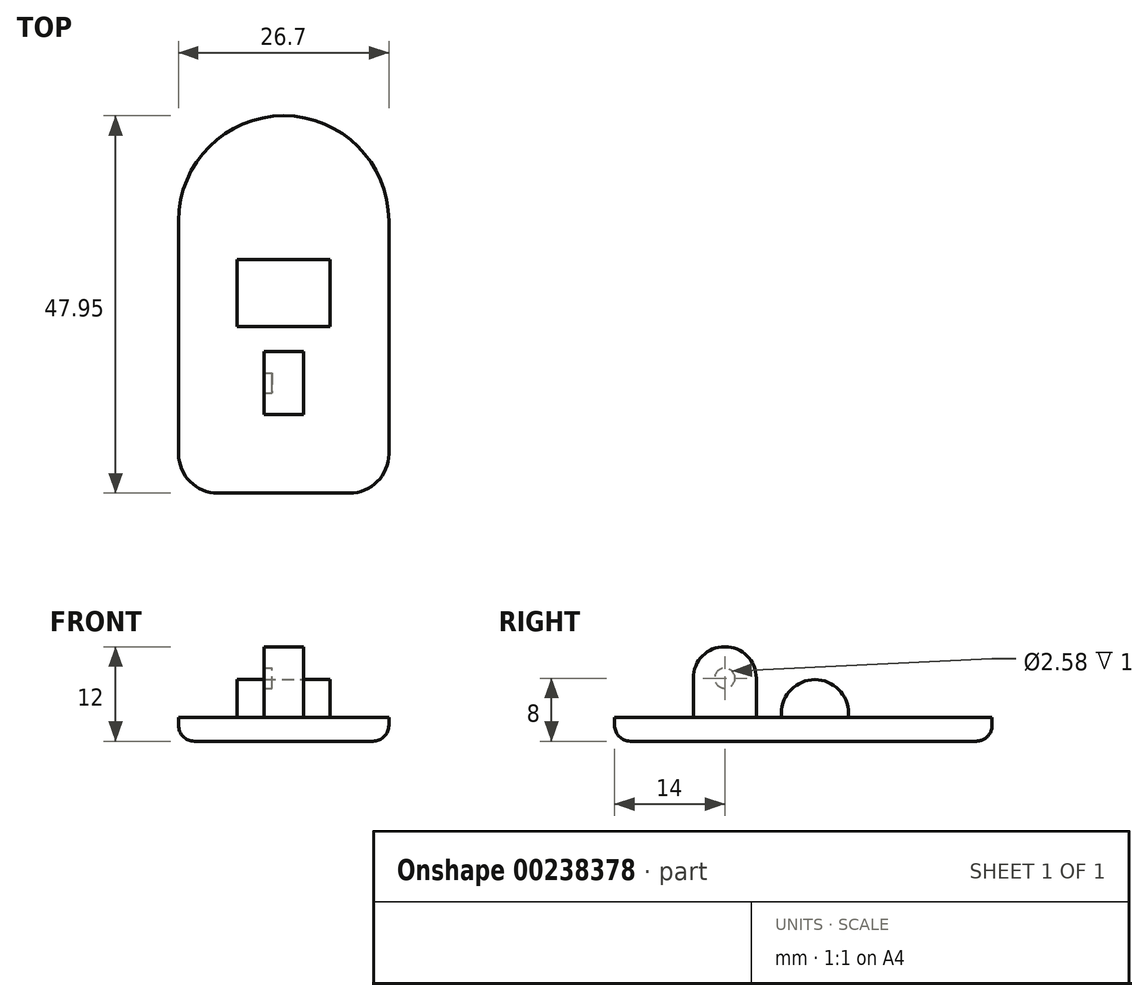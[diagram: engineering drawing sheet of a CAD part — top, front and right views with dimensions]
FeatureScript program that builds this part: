
annotation { "Feature Type Name" : "Feature", "Feature Type Description" : "" }
export const myFeature = defineFeature(function(context is Context, id is Id, definition is map)
    precondition{}
    {
        {
            var Q0;
            Q0=qCreatedBy(makeId("Top.planeOp"),FACE);
            var sketch = newSketch(context, id + "F0", { "sketchPlane" : qUnion([Q0])});
            skArc(sketch, "E0", {"start": v(13.35, 0) * mm, "mid": v(0, 13.35) * mm, "end": v(-13.35, 0) * mm});
            skLineSegment(sketch, "E1", {"start": v(-13.35, 0) * mm, "end": v(-13.35, -34.6) * mm});
            skLineSegment(sketch, "E2", {"start": v(13.35, 0) * mm, "end": v(13.35, -34.6) * mm});
            skLineSegment(sketch, "E3", {"start": v(13.35, -34.6) * mm, "end": v(-13.35, -34.6) * mm});
            skLineSegment(sketch, "E4", {"start": v(0, -34.6) * mm, "end": v(0, 13.35) * mm});
            skLineSegment(sketch, "E5", {"start": v(-13.35, -24.6) * mm, "end": v(13.35, -24.6) * mm});
            skLineSegment(sketch, "E6", {"start": v(-13.35, -16.6) * mm, "end": v(13.35, -16.6) * mm});
            skLineSegment(sketch, "E7", {"start": v(-2.5, -16.6) * mm, "end": v(-2.5, -34.6) * mm});
            skLineSegment(sketch, "E8", {"start": v(2.5, -16.6) * mm, "end": v(2.5, -34.6) * mm});
            skPoint(sketch, "E9.orphan", {"position": v(-2.5, 0) * mm});
            skPoint(sketch, "E10.orphan", {"position": v(2.5, 0) * mm});
            skLineSegment(sketch, "E11", {"start": v(-5.9, 0) * mm, "end": v(-5.9, -16.6) * mm});
            skLineSegment(sketch, "E12", {"start": v(5.9, 0) * mm, "end": v(5.9, -16.6) * mm});
            skLineSegment(sketch, "E13", {"start": v(-13.35, -4.9) * mm, "end": v(13.35, -4.9) * mm});
            skLineSegment(sketch, "E14", {"start": v(-13.35, -13.4) * mm, "end": v(13.35, -13.4) * mm});
            skSolve(sketch);
        }
        {
            var Q0;
            {var subQ4=sQuery(id+"F0.wireOp",EDGE,"E1");var subQ6=sQuery(id+"F0.wireOp",EDGE,"E5");var subQ7=makeQuery(id+"F0.imprint","INTERSECT",VERTEX,{"derivedFrom":[subQ4,subQ6]});Q0=makeQuery(id+"F0.imprint","IMPRINT",FACE,{"disambiguationData":[TD([[makeQuery(id+"F0.imprint","IMPRINT",EDGE,{"disambiguationData":[TD([[subQ7,1.0]])],"derivedFrom":subQ4}),1.0]])]});}
            var Q1;
            {var subQ0=sQuery(id+"F0.wireOp",EDGE,"E3");var subQ1=sQuery(id+"F0.wireOp",EDGE,"E1");var subQ2=makeQuery(id+"F0.imprint","INTERSECT",VERTEX,{"derivedFrom":[subQ1,subQ0]});Q1=makeQuery(id+"F0.imprint","IMPRINT",FACE,{"disambiguationData":[TD([[makeQuery(id+"F0.imprint","IMPRINT",EDGE,{"disambiguationData":[TD([[subQ2,1.0]])],"derivedFrom":subQ1}),1.0]])]});}
            var Q2;
            {var subQ0=sQuery(id+"F0.wireOp",EDGE,"E4");var subQ1=sQuery(id+"F0.wireOp",EDGE,"E3");var subQ2=makeQuery(id+"F0.imprint","INTERSECT",VERTEX,{"derivedFrom":[subQ1,subQ0]});Q2=makeQuery(id+"F0.imprint","IMPRINT",FACE,{"disambiguationData":[TD([[makeQuery(id+"F0.imprint","IMPRINT",EDGE,{"disambiguationData":[TD([[subQ2,1.0]])],"derivedFrom":subQ1}),-1.0]])]});}
            var Q3;
            {var subQ0=sQuery(id+"F0.wireOp",EDGE,"E4");var subQ1=sQuery(id+"F0.wireOp",EDGE,"E3");var subQ2=makeQuery(id+"F0.imprint","INTERSECT",VERTEX,{"derivedFrom":[subQ1,subQ0]});Q3=makeQuery(id+"F0.imprint","IMPRINT",FACE,{"disambiguationData":[TD([[makeQuery(id+"F0.imprint","IMPRINT",EDGE,{"disambiguationData":[TD([[subQ2,-1.0]])],"derivedFrom":subQ1}),-1.0]])]});}
            var Q4;
            {var subQ0=sQuery(id+"F0.wireOp",EDGE,"E5");var subQ1=sQuery(id+"F0.wireOp",EDGE,"E4");var subQ2=makeQuery(id+"F0.imprint","INTERSECT",VERTEX,{"derivedFrom":[subQ1,subQ0]});Q4=makeQuery(id+"F0.imprint","IMPRINT",FACE,{"disambiguationData":[TD([[makeQuery(id+"F0.imprint","IMPRINT",EDGE,{"disambiguationData":[TD([[subQ2,-1.0]])],"derivedFrom":subQ1}),1.0]])]});}
            var Q5;
            {var subQ0=sQuery(id+"F0.wireOp",EDGE,"E5");var subQ1=sQuery(id+"F0.wireOp",EDGE,"E4");var subQ2=makeQuery(id+"F0.imprint","INTERSECT",VERTEX,{"derivedFrom":[subQ1,subQ0]});Q5=makeQuery(id+"F0.imprint","IMPRINT",FACE,{"disambiguationData":[TD([[makeQuery(id+"F0.imprint","IMPRINT",EDGE,{"disambiguationData":[TD([[subQ2,-1.0]])],"derivedFrom":subQ1}),-1.0]])]});}
            var Q6;
            {var subQ1=sQuery(id+"F0.wireOp",EDGE,"E2");var subQ4=sQuery(id+"F0.wireOp",EDGE,"E5");var subQ5=makeQuery(id+"F0.imprint","INTERSECT",VERTEX,{"derivedFrom":[subQ1,subQ4]});Q6=makeQuery(id+"F0.imprint","IMPRINT",FACE,{"disambiguationData":[TD([[makeQuery(id+"F0.imprint","IMPRINT",EDGE,{"disambiguationData":[TD([[subQ5,1.0]])],"derivedFrom":subQ1}),-1.0]])]});}
            var Q7;
            {var subQ0=sQuery(id+"F0.wireOp",EDGE,"E3");var subQ1=sQuery(id+"F0.wireOp",EDGE,"E2");var subQ2=makeQuery(id+"F0.imprint","INTERSECT",VERTEX,{"derivedFrom":[subQ1,subQ0]});Q7=makeQuery(id+"F0.imprint","IMPRINT",FACE,{"disambiguationData":[TD([[makeQuery(id+"F0.imprint","IMPRINT",EDGE,{"disambiguationData":[TD([[subQ2,1.0]])],"derivedFrom":subQ1}),-1.0]])]});}
            var Q8;
            {var subQ0=sQuery(id+"F0.wireOp",EDGE,"E6");var subQ4=sQuery(id+"F0.wireOp",EDGE,"E4");var subQ5=makeQuery(id+"F0.imprint","INTERSECT",VERTEX,{"derivedFrom":[subQ4,subQ0]});Q8=makeQuery(id+"F0.imprint","IMPRINT",FACE,{"disambiguationData":[TD([[makeQuery(id+"F0.imprint","IMPRINT",EDGE,{"disambiguationData":[TD([[subQ5,-1.0]])],"derivedFrom":subQ4}),-1.0]])]});}
            var Q9;
            {var subQ0=sQuery(id+"F0.wireOp",EDGE,"E6");var subQ1=sQuery(id+"F0.wireOp",EDGE,"E2");var subQ2=makeQuery(id+"F0.imprint","INTERSECT",VERTEX,{"derivedFrom":[subQ1,subQ0]});Q9=makeQuery(id+"F0.imprint","IMPRINT",FACE,{"disambiguationData":[TD([[makeQuery(id+"F0.imprint","IMPRINT",EDGE,{"disambiguationData":[TD([[subQ2,1.0]])],"derivedFrom":subQ1}),-1.0]])]});}
            var Q10;
            {var subQ1=sQuery(id+"F0.wireOp",EDGE,"E6");var subQ6=sQuery(id+"F0.wireOp",EDGE,"E4");var subQ7=makeQuery(id+"F0.imprint","INTERSECT",VERTEX,{"derivedFrom":[subQ6,subQ1]});Q10=makeQuery(id+"F0.imprint","IMPRINT",FACE,{"disambiguationData":[TD([[makeQuery(id+"F0.imprint","IMPRINT",EDGE,{"disambiguationData":[TD([[subQ7,-1.0]])],"derivedFrom":subQ6}),1.0]])]});}
            var Q11;
            {var subQ0=sQuery(id+"F0.wireOp",EDGE,"E6");var subQ1=sQuery(id+"F0.wireOp",EDGE,"E1");var subQ2=makeQuery(id+"F0.imprint","INTERSECT",VERTEX,{"derivedFrom":[subQ1,subQ0]});Q11=makeQuery(id+"F0.imprint","IMPRINT",FACE,{"disambiguationData":[TD([[makeQuery(id+"F0.imprint","IMPRINT",EDGE,{"disambiguationData":[TD([[subQ2,1.0]])],"derivedFrom":subQ1}),1.0]])]});}
            var Q12;
            {var subQ0=sQuery(id+"F0.wireOp",EDGE,"E13");var subQ1=sQuery(id+"F0.wireOp",EDGE,"E1");var subQ2=makeQuery(id+"F0.imprint","INTERSECT",VERTEX,{"derivedFrom":[subQ1,subQ0]});Q12=makeQuery(id+"F0.imprint","IMPRINT",FACE,{"disambiguationData":[TD([[makeQuery(id+"F0.imprint","IMPRINT",EDGE,{"disambiguationData":[TD([[subQ2,-1.0]])],"derivedFrom":subQ1}),1.0]])]});}
            var Q13;
            {var subQ0=sQuery(id+"F0.wireOp",EDGE,"E14");var subQ1=sQuery(id+"F0.wireOp",EDGE,"E4");var subQ2=makeQuery(id+"F0.imprint","INTERSECT",VERTEX,{"derivedFrom":[subQ1,subQ0]});Q13=makeQuery(id+"F0.imprint","IMPRINT",FACE,{"disambiguationData":[TD([[makeQuery(id+"F0.imprint","IMPRINT",EDGE,{"disambiguationData":[TD([[subQ2,-1.0]])],"derivedFrom":subQ1}),1.0]])]});}
            var Q14;
            {var subQ0=sQuery(id+"F0.wireOp",EDGE,"E14");var subQ1=sQuery(id+"F0.wireOp",EDGE,"E4");var subQ2=makeQuery(id+"F0.imprint","INTERSECT",VERTEX,{"derivedFrom":[subQ1,subQ0]});Q14=makeQuery(id+"F0.imprint","IMPRINT",FACE,{"disambiguationData":[TD([[makeQuery(id+"F0.imprint","IMPRINT",EDGE,{"disambiguationData":[TD([[subQ2,-1.0]])],"derivedFrom":subQ1}),-1.0]])]});}
            var Q15;
            {var subQ0=sQuery(id+"F0.wireOp",EDGE,"E13");var subQ1=sQuery(id+"F0.wireOp",EDGE,"E2");var subQ2=makeQuery(id+"F0.imprint","INTERSECT",VERTEX,{"derivedFrom":[subQ1,subQ0]});Q15=makeQuery(id+"F0.imprint","IMPRINT",FACE,{"disambiguationData":[TD([[makeQuery(id+"F0.imprint","IMPRINT",EDGE,{"disambiguationData":[TD([[subQ2,-1.0]])],"derivedFrom":subQ1}),-1.0]])]});}
            var Q16;
            {var subQ4=sQuery(id+"F0.wireOp",EDGE,"E0");var subQ6=sQuery(id+"F0.wireOp",EDGE,"E2");var subQ7=makeQuery(id+"F0.imprint","INTERSECT",VERTEX,{"derivedFrom":[subQ4,subQ6]});Q16=makeQuery(id+"F0.imprint","IMPRINT",FACE,{"disambiguationData":[TD([[makeQuery(id+"F0.imprint","IMPRINT",EDGE,{"disambiguationData":[TD([[subQ7,-1.0]])],"derivedFrom":subQ4}),1.0]])]});}
            var Q17;
            {var subQ1=sQuery(id+"F0.wireOp",EDGE,"E0");var subQ5=sQuery(id+"F0.wireOp",EDGE,"E1");var subQ8=makeQuery(id+"F0.imprint","INTERSECT",VERTEX,{"derivedFrom":[subQ1,subQ5]});Q17=makeQuery(id+"F0.imprint","IMPRINT",FACE,{"disambiguationData":[TD([[makeQuery(id+"F0.imprint","IMPRINT",EDGE,{"disambiguationData":[TD([[subQ8,1.0]])],"derivedFrom":subQ1}),1.0]])]});}
            extrude(context, id + "F1", {"entities" : qUnion([Q0, Q1, Q2, Q3, Q4, Q5, Q6, Q7, Q8, Q9, Q10, Q11, Q12, Q13, Q14, Q15, Q16, Q17]), "oppositeDirection" : true, "depth" : 3 * mm});
        }
        {
            var Q0;
            {var subQ0=sQuery(id+"F0.wireOp",EDGE,"E14");var subQ1=sQuery(id+"F0.wireOp",EDGE,"E4");var subQ2=makeQuery(id+"F0.imprint","INTERSECT",VERTEX,{"derivedFrom":[subQ1,subQ0]});Q0=makeQuery(id+"F0.imprint","IMPRINT",FACE,{"disambiguationData":[TD([[makeQuery(id+"F0.imprint","IMPRINT",EDGE,{"disambiguationData":[TD([[subQ2,-1.0]])],"derivedFrom":subQ1}),1.0]])]});}
            var Q1;
            {var subQ0=sQuery(id+"F0.wireOp",EDGE,"E14");var subQ1=sQuery(id+"F0.wireOp",EDGE,"E4");var subQ2=makeQuery(id+"F0.imprint","INTERSECT",VERTEX,{"derivedFrom":[subQ1,subQ0]});Q1=makeQuery(id+"F0.imprint","IMPRINT",FACE,{"disambiguationData":[TD([[makeQuery(id+"F0.imprint","IMPRINT",EDGE,{"disambiguationData":[TD([[subQ2,-1.0]])],"derivedFrom":subQ1}),-1.0]])]});}
            extrude(context, id + "F2", {"entities" : qUnion([Q0, Q1]), "operationType" : NewBodyOperationType.ADD, "depth" : .563 * mm});
        }
        {
            var Q0;
            {var subQ0=sQuery(id+"F0.wireOp",EDGE,"E5");var subQ1=sQuery(id+"F0.wireOp",EDGE,"E4");var subQ2=makeQuery(id+"F0.imprint","INTERSECT",VERTEX,{"derivedFrom":[subQ1,subQ0]});Q0=makeQuery(id+"F0.imprint","IMPRINT",FACE,{"disambiguationData":[TD([[makeQuery(id+"F0.imprint","IMPRINT",EDGE,{"disambiguationData":[TD([[subQ2,-1.0]])],"derivedFrom":subQ1}),-1.0]])]});}
            var Q1;
            {var subQ0=sQuery(id+"F0.wireOp",EDGE,"E5");var subQ1=sQuery(id+"F0.wireOp",EDGE,"E4");var subQ2=makeQuery(id+"F0.imprint","INTERSECT",VERTEX,{"derivedFrom":[subQ1,subQ0]});Q1=makeQuery(id+"F0.imprint","IMPRINT",FACE,{"disambiguationData":[TD([[makeQuery(id+"F0.imprint","IMPRINT",EDGE,{"disambiguationData":[TD([[subQ2,-1.0]])],"derivedFrom":subQ1}),1.0]])]});}
            extrude(context, id + "F3", {"entities" : qUnion([Q0, Q1]), "operationType" : NewBodyOperationType.ADD, "depth" : 5 * mm});
        }
        {
            var Q0;
            Q0=makeQuery(id+"F3.opExtrude","SWEPT_FACE",FACE,{"disambiguationData":[OSD([sQuery(id+"F0.wireOp",EDGE,"E8")])]});
            var sketch = newSketch(context, id + "F4", { "sketchPlane" : qUnion([Q0])});
            skCircle(sketch, "E15", {"center": v(-20.6, 5) * mm, "radius": 4 * mm});
            skCircle(sketch, "E16", {"center": v(-20.6, 5) * mm, "radius": 1.29 * mm});
            skSolve(sketch);
        }
        {
            var Q0;
            Q0=makeQuery(id+"F2.opExtrude","SWEPT_FACE",FACE,{"disambiguationData":[OSD([sQuery(id+"F0.wireOp",EDGE,"E12")])]});
            var sketch = newSketch(context, id + "F5", { "sketchPlane" : qUnion([Q0])});
            skCircle(sketch, "E17", {"center": v(-9.15, 0.56) * mm, "radius": 4.25 * mm});
            skSolve(sketch);
        }
        {
            var Q0;
            {var subQ1=sQuery(id+"F0.wireOp",EDGE,"E12");var subQ2=makeQuery(id+"F2.opExtrude","CAP_EDGE",EDGE,{"disambiguationData":[OSD([subQ1])],"isStart":false});Q0=makeQuery(id+"F5.imprint","IMPRINT",FACE,{"disambiguationData":[TD([[makeQuery(id+"F5.imprint","IMPRINT",EDGE,{"derivedFrom":subQ2}),-1.0]])]});}
            extrude(context, id + "F6", {"entities" : qUnion([Q0]), "operationType" : NewBodyOperationType.ADD, "oppositeDirection" : true, "depth" : 11.8 * mm});
        }
        {
            var Q0;
            {var subQ1=sQuery(id+"F0.wireOp",EDGE,"E8");var subQ2=makeQuery(id+"F3.opExtrude","CAP_EDGE",EDGE,{"disambiguationData":[OSD([subQ1])],"isStart":false});Q0=makeQuery(id+"F4.imprint","IMPRINT",FACE,{"disambiguationData":[TD([[makeQuery(id+"F4.imprint","IMPRINT",EDGE,{"derivedFrom":subQ2}),-1.0]])]});}
            extrude(context, id + "F7", {"entities" : qUnion([Q0]), "operationType" : NewBodyOperationType.ADD, "oppositeDirection" : true, "depth" : 5 * mm});
        }
        {
            var Q0;
            {var subQ0=sQuery(id+"F4.wireOp",EDGE,"E16");var subQ1=makeQuery(id+"F3.opExtrude","CAP_EDGE",EDGE,{"disambiguationData":[OSD([sQuery(id+"F0.wireOp",EDGE,"E8")])],"isStart":false});var subQ2=makeQuery(id+"F4.imprint","INTERSECT",VERTEX,{"disambiguationData":[OD(0.0)],"derivedFrom":[subQ1,subQ0]});Q0=makeQuery(id+"F4.imprint","IMPRINT",FACE,{"disambiguationData":[TD([[makeQuery(id+"F4.imprint","IMPRINT",EDGE,{"disambiguationData":[TD([[subQ2,1.0]])],"derivedFrom":subQ0}),1.0]])]});}
            var Q1;
            {var subQ0=sQuery(id+"F4.wireOp",EDGE,"E16");var subQ1=makeQuery(id+"F3.opExtrude","CAP_EDGE",EDGE,{"disambiguationData":[OSD([sQuery(id+"F0.wireOp",EDGE,"E8")])],"isStart":false});var subQ2=makeQuery(id+"F4.imprint","INTERSECT",VERTEX,{"disambiguationData":[OD(0.0)],"derivedFrom":[subQ1,subQ0]});Q1=makeQuery(id+"F4.imprint","IMPRINT",FACE,{"disambiguationData":[TD([[makeQuery(id+"F4.imprint","IMPRINT",EDGE,{"disambiguationData":[TD([[subQ2,-1.0]])],"derivedFrom":subQ0}),1.0]])]});}
            extrude(context, id + "F8", {"entities" : qUnion([Q0, Q1]), "operationType" : NewBodyOperationType.REMOVE, "oppositeDirection" : true, "depth" : 25 * mm});
        }
        {
            var Q0;
            {var subQ0=sQuery(id+"F0.wireOp",EDGE,"E8");Q0=makeQuery(id+"F7.boolean.opBoolean","MERGE",FACE,{"derivedFrom":[makeQuery(id+"F3.opExtrude","SWEPT_FACE",FACE,{"disambiguationData":[OSD([subQ0])]}),makeQuery(id+"F7.opExtrude","CAP_FACE",FACE,{"disambiguationData":[OSD([subQ0,sQuery(id+"F4.wireOp",EDGE,"E15"),sQuery(id+"F4.wireOp",EDGE,"E16")])],"isStart":true})]});}
            var sketch = newSketch(context, id + "F9", { "sketchPlane" : qUnion([Q0])});
            skCircle(sketch, "E18", {"center": v(-20.6, 5) * mm, "radius": 2.06 * mm});
            skSolve(sketch);
        }
        {
            var Q0;
            Q0 = qSketchRegion(id + "F9", true);
            extrude(context, id + "F10", {"entities" : qUnion([Q0]), "operationType" : NewBodyOperationType.ADD, "oppositeDirection" : true, "depth" : 1 * mm});
        }
        {
            var Q0;
            Q0=makeQuery(id+"F1.opExtrude","SWEPT_EDGE",EDGE,{"disambiguationData":[OSD([sQuery(id+"F0.wireOp",EDGE,"E2"),sQuery(id+"F0.wireOp",EDGE,"E3")])]});
            fillet(context, id + "F11", {"entities" : qUnion([Q0]), "radius" : 5 * mm, "tangentPropagation" : true, "allowEdgeOverflow" : false});
        }
        {
            var Q0;
            Q0=makeQuery(id+"F1.opExtrude","SWEPT_EDGE",EDGE,{"disambiguationData":[OSD([sQuery(id+"F0.wireOp",EDGE,"E1"),sQuery(id+"F0.wireOp",EDGE,"E3")])]});
            fillet(context, id + "F12", {"entities" : qUnion([Q0]), "radius" : 5 * mm, "tangentPropagation" : true, "allowEdgeOverflow" : false});
        }
        {
            var Q0;
            Q0=makeQuery(id+"F1.opExtrude","CAP_EDGE",EDGE,{"disambiguationData":[OSD([sQuery(id+"F0.wireOp",EDGE,"E3")])],"isStart":false});
            fillet(context, id + "F13", {"entities" : qUnion([Q0]), "radius" : 2 * mm, "tangentPropagation" : true, "allowEdgeOverflow" : false});
        }
        {
            var Q0;
            Q0=makeQuery(id+"F10.opExtrude","CAP_FACE",FACE,{"disambiguationData":[OSD([sQuery(id+"F9.wireOp",EDGE,"E18")])],"isStart":false});
            extrude(context, id + "F14", {"entities" : qUnion([Q0]), "operationType" : NewBodyOperationType.ADD, "depth" : 3 * mm});
        }
    });
